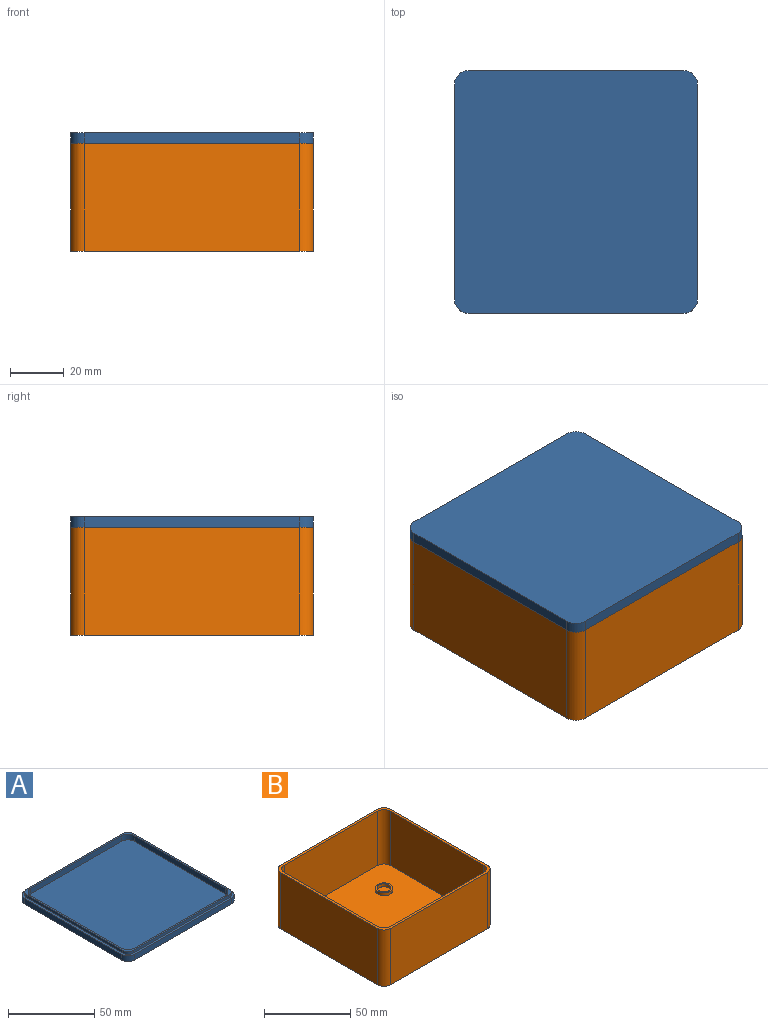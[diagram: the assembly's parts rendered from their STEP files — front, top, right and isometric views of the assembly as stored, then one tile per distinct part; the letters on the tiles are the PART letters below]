
ASSEMBLY  parts=2 mates=1
PART A: 28 faces, bbox 90x90x6 mm
  f0: plane 87.4x87.4mm, normal (0,0,1), area 417.6mm2, adj f1,f2,f3,f4,f6,f7,f8,f9
  f1: plane 74.84x4mm, normal (0,1,0), area 299.4mm2, adj f0,f5,f6,f9
  f2: plane 74.84x4mm, normal (-1,0,0), area 299.4mm2, adj f0,f5,f6,f7
  f3: plane 74.84x4mm, normal (0,-1,0), area 299.4mm2, adj f0,f5,f7,f8
  f4: plane 74.84x4mm, normal (1,0,0), area 299.4mm2, adj f0,f5,f8,f9
  f5: plane 85x85mm, normal (0,0,1), area 7202.8mm2, adj f1,f2,f3,f4,f6,f7,f8,f9
  f6: cylinder r=5.08mm len=5.08mm, axis (0,0,1), area 31.9mm2, adj f0,f1,f2,f5
  f7: cylinder r=5.08mm len=5.08mm, axis (0,0,-1), area 31.9mm2, adj f0,f2,f3,f5
  f8: cylinder r=5.08mm len=5.08mm, axis (0,0,1), area 31.9mm2, adj f0,f3,f4,f5
  f9: cylinder r=5.08mm len=5.08mm, axis (0,0,-1), area 31.9mm2, adj f0,f1,f4,f5
  f10: cylinder r=4.62mm len=4.62mm, axis (0,0,1), area 14.5mm2, adj f0,f11,f17,f18
  f11: plane 78.16x2mm, normal (1,0,0), area 156.3mm2, adj f0,f10,f12,f18
  f12: cylinder r=4.62mm len=4.62mm, axis (0,0,1), area 14.5mm2, adj f0,f11,f13,f18
  f13: plane 78.16x2mm, normal (0,-1,0), area 156.3mm2, adj f0,f12,f14,f18
  f14: cylinder r=4.62mm len=4.62mm, axis (0,0,1), area 14.5mm2, adj f0,f13,f15,f18
  f15: plane 78.16x2mm, normal (-1,0,0), area 156.3mm2, adj f0,f14,f16,f18
  f16: cylinder r=4.62mm len=4.62mm, axis (0,0,1), area 14.5mm2, adj f0,f15,f17,f18
  f17: plane 78.16x2mm, normal (0,1,0), area 156.3mm2, adj f0,f10,f16,f18
  f18: plane 90x90mm, normal (0,0,1), area 457.4mm2, adj f10,f11,f12,f13,f14,f15,f16,f17
  f19: plane 90x90mm, normal (0,0,-1), area 8077.8mm2, adj f20,f21,f22,f23,f24,f25,f26,f27
  f20: cylinder r=5.08mm len=5.08mm, axis (0,0,1), area 31.9mm2, adj f18,f19,f22,f24
  f21: cylinder r=5.08mm len=5.08mm, axis (0,0,-1), area 31.9mm2, adj f18,f19,f22,f27
  f22: plane 79.84x4mm, normal (-1,0,0), area 319.4mm2, adj f18,f19,f20,f21
  f23: cylinder r=5.08mm len=5.08mm, axis (0,0,-1), area 31.9mm2, adj f18,f19,f24,f26
  f24: plane 79.84x4mm, normal (0,1,0), area 319.4mm2, adj f18,f19,f20,f23
  f25: cylinder r=5.08mm len=5.08mm, axis (0,0,1), area 31.9mm2, adj f18,f19,f26,f27
  f26: plane 79.84x4mm, normal (1,0,0), area 319.4mm2, adj f18,f19,f23,f25
  f27: plane 79.84x4mm, normal (0,-1,0), area 319.4mm2, adj f18,f19,f21,f25
PART B: 35 faces, bbox 90x90x40 mm
  f0: plane 90x90mm, normal (0,0,1), area 531mm2, adj f1,f2,f3,f4,f6,f7,f8,f9
  f1: plane 79.84x40mm, normal (0,-1,0), area 3193.6mm2, adj f0,f5,f31,f34
  f2: plane 79.84x40mm, normal (1,0,0), area 3193.6mm2, adj f0,f5,f31,f32
  f3: plane 79.84x40mm, normal (0,1,0), area 3193.6mm2, adj f0,f5,f32,f33
  f4: plane 79.84x40mm, normal (-1,0,0), area 3193.6mm2, adj f0,f5,f33,f34
  f5: plane 90x90mm, normal (0,0,-1), area 8077.8mm2, adj f1,f2,f3,f4,f31,f32,f33,f34
  f6: plane 76.84x38.5mm, normal (0,1,0), area 2958.3mm2, adj f0,f10,f27,f30
  f7: plane 76.84x38.5mm, normal (-1,0,0), area 2958.3mm2, adj f0,f10,f27,f28
  f8: plane 76.84x38.5mm, normal (0,-1,0), area 2958.3mm2, adj f0,f10,f28,f29
  f9: plane 76.84x38.5mm, normal (1,0,0), area 2958.3mm2, adj f0,f10,f29,f30
  f10: plane 87x87mm, normal (0,0,1), area 7232.7mm2, adj f6,f7,f8,f9,f12,f16,f20,f24
  f11: cylinder r=4mm len=8mm, axis (0,0,-1), area 50.3mm2, adj f13,f14
  f12: cylinder r=5mm len=10mm, axis (0,0,-1), area 62.8mm2, adj f10,f13
  f13: plane 10x10mm, normal (0,0,1), area 28.3mm2, adj f11,f12
  f14: plane 8x8mm, normal (0,0,1), area 50.3mm2, adj f11
  f15: cylinder r=4mm len=8mm, axis (0,0,-1), area 50.3mm2, adj f17,f18
  f16: cylinder r=5mm len=10mm, axis (0,0,-1), area 62.8mm2, adj f10,f17
  f17: plane 10x10mm, normal (0,0,1), area 28.3mm2, adj f15,f16
  f18: plane 8x8mm, normal (0,0,1), area 50.3mm2, adj f15
  f19: cylinder r=4mm len=8mm, axis (0,0,-1), area 50.3mm2, adj f21,f22
  f20: cylinder r=5mm len=10mm, axis (0,0,-1), area 62.8mm2, adj f10,f21
  f21: plane 10x10mm, normal (0,0,1), area 28.3mm2, adj f19,f20
  f22: plane 8x8mm, normal (0,0,1), area 50.3mm2, adj f19
  f23: cylinder r=4mm len=8mm, axis (0,0,-1), area 50.3mm2, adj f25,f26
  f24: cylinder r=5mm len=10mm, axis (0,0,-1), area 62.8mm2, adj f10,f25
  f25: plane 10x10mm, normal (0,0,1), area 28.3mm2, adj f23,f24
  f26: plane 8x8mm, normal (0,0,1), area 50.3mm2, adj f23
  f27: cylinder r=5.08mm len=38.5mm, axis (0,0,1), area 307.2mm2, adj f0,f6,f7,f10
  f28: cylinder r=5.08mm len=38.5mm, axis (0,0,-1), area 307.2mm2, adj f0,f7,f8,f10
  f29: cylinder r=5.08mm len=38.5mm, axis (0,0,1), area 307.2mm2, adj f0,f8,f9,f10
  f30: cylinder r=5.08mm len=38.5mm, axis (0,0,-1), area 307.2mm2, adj f0,f6,f9,f10
  f31: cylinder r=5.08mm len=40mm, axis (0,0,1), area 319.2mm2, adj f0,f1,f2,f5
  f32: cylinder r=5.08mm len=40mm, axis (0,0,-1), area 319.2mm2, adj f0,f2,f3,f5
  f33: cylinder r=5.08mm len=40mm, axis (0,0,1), area 319.2mm2, adj f0,f3,f4,f5
  f34: cylinder r=5.08mm len=40mm, axis (0,0,-1), area 319.2mm2, adj f0,f1,f4,f5
PLACE A rot(axis=(1,0,0),180deg) t=(-0.11,6.08,25.3)mm
PLACE B t=(-0.11,6.08,-18.7)mm
MATE parallel A.f18 <-> B.f0  axis (0,0,-1) through (-0.11,6.08,21.3)mm
